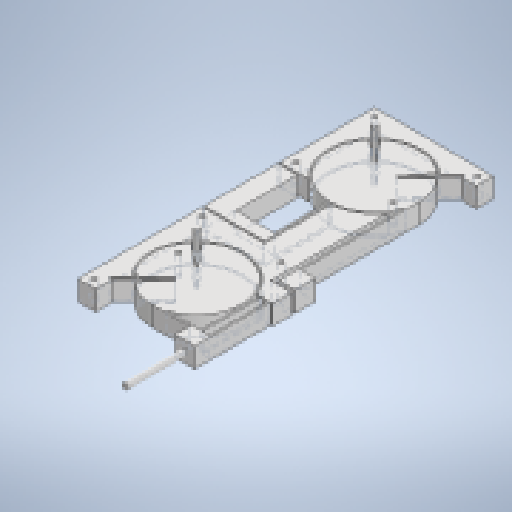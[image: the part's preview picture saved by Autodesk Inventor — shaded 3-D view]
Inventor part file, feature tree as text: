
AUTODESK INVENTOR PART (.ipt)
format: ipt  version: 2023 (Build 270158000, 158)  size: 387,584 bytes
history: native  units: mm
features: extrude x5, sketch x4, other x3, reference x2
ambient origin geometry x8: Origin, YZ Plane, XZ Plane, XY Plane, X Axis, Y Axis, Z Axis, Center Point
bodies: Solid1 (feature_tree)
feature tree (14):
  extrude  "Extrusion1"  Depth=150.0mm
  extrude  "Extrusion2"  Depth=20.0mm
  extrude  "Extrusion3"  Depth=150.0mm
  extrude  "Extrusion4"  Depth=45.0mm
  extrude  "Extrusion5"  Depth=45.0mm
  sketch  "Sketch1"  dims[d0=100.0mm d1=150.0mm]
  sketch  "Sketch6"  dims[d2=20.0mm d3=20.0mm]
  sketch  "Sketch7"  dims[d4=150.0mm d5=150.0mm]
  reference  "Reference1"
  reference  "Reference2"
  sketch  "Sketch8"  dims[d6=10.0mm d7=0.0mm d18=45.0mm d19=45.0mm d21=47.0mm d22=47.0mm d23=1.0mm d24=1.0mm d25=10.0mm d26=30.0mm d27=1.0mm d28=1.0mm d29=1.0mm d31=50.0mm d32=7.5mm d34=2.0mm d35=2.0mm d36=0.5mm d37=0.5mm d39=3.0mm d40=3.0mm d41=45.0deg d43=30.0mm d44=45.0deg d45=10.0mm d46=1.0mm d47=1.0mm d48=1.0mm d49=0.5mm d50=0.5mm d51=1.0mm d52=1.0mm d53=8.5mm d58=0.5mm d59=0.5mm d60=1.0mm d61=1.0mm d62=0.5mm d63=0.5mm d64=1.0mm d65=1.0mm d66=8.5mm d67=8.5mm d68=30.0mm d69=30.0mm d70=30.0mm d71=8.5mm d72=8.5mm d73=0.5mm d74=0.5mm d75=1.0mm d76=1.0mm d77=0.872665mm d78=0.872665mm d79=0.872665mm d80=0.872665mm d81=0.872665mm d82=0.872665mm d83=0.872665mm d84=0.872665mm d85=20.0mm d86=0.0mm d94=4.0mm d95=4.0mm d96=2.65mm d97=4.0mm d98=4.0mm d99=2.65mm d100=0.0mm d101=2.65mm d102=40.0mm d103=2.65mm d104=2.65mm d105=2.65mm d106=4.0mm d107=4.0mm d108=4.0mm d109=4.0mm d110=4.0mm d111=4.0mm d112=10.0mm d113=0.0mm d114=2.65mm d115=2.65mm d116=10.0mm d117=0.0mm d118=3.0mm d119=5.0mm d120=5.0mm d121=30.0mm d122=0.0mm]
  other  "<userpath>\ClawdDrive\Objet3D\IminaProbe\V2\FlexK7V2.iam"
  other  "FlexK7V2.iam"
  other  "FlexK7Holder:1"
